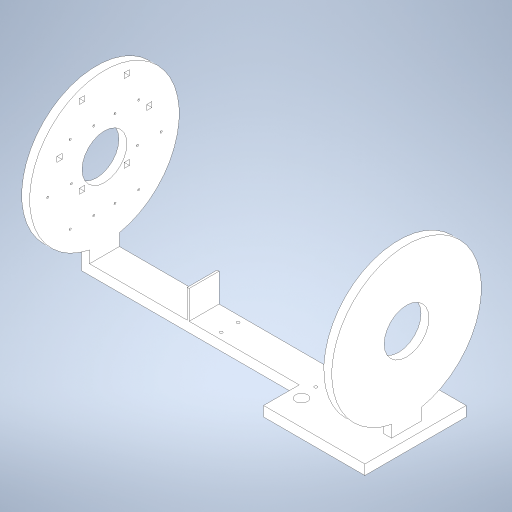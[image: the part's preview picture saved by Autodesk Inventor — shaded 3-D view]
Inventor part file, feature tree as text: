
AUTODESK INVENTOR PART (.ipt)
format: ipt  version: 2023 (Build 270158000, 158)  size: 558,592 bytes
history: native  units: in
note: dims shown in document units (in); Inventor stores cm internally (conversion verified against a paired STEP export)
features: extrude x12, sketch x5, projected_geometry x2, pattern_linear x1
ambient origin geometry x8: Origin, YZ Plane, XZ Plane, XY Plane, X Axis, Y Axis, Z Axis, Center Point
bodies: Solid1 (feature_tree)
feature tree (20):
  extrude  "Extrusion1"  Depth=0.2047in
  extrude  "Extrusion2"  Depth=0.2047in TaperAngle=360.0deg
  extrude  "Extrusion3"  Depth=0.315in
  sketch  "Sketch2"  dims[d31=0.2047in d32=2.3622in d34=360.0deg]
  extrude  "Extrusion4"  Depth=0.2047in
  extrude  "Extrusion5"  Depth=0.315in
  pattern_linear  "Rectangular Pattern1"  Spacing1=0.2047in  [1 undecoded]
  extrude  "Extrusion7"  Depth=0.2047in
  extrude  "Extrusion8"  Depth=0.2717in
  extrude  "Extrusion9"  Depth=0.2717in
  sketch  "Sketch7"  dims[d40=0.315in d41=0.315in d42=0.2047in d43=0.2047in d44=0.8465in d45=4.3307in d46=2.7559in d47=0.5906in d49=0.315in d50=1.122in d51=0.3937in d52=0.315in d53=0.0in d54=0.3937in d55=0.0in d56=12.5984in d57=0.0in d58=4.0in d59=4.0in d60=0.4724in d63=0.2559in d65=3.937in d66=1.0039in d67=0.3346in d68=0.1181in d69=0.7874in d71=3.7402in d72=0.3937in d74=0.3937in d76=0.3937in d77=0.0in d78=0.3937in d79=0.0in d80=1.0in d81=0.5in d82=3.0118in d83=0.3937in d84=0.0in d85=0.7874in d87=11.9291in d88=0.122in d89=0.0in d90=0.122in d91=0.0in d92=0.0787in d93=1.5157in d94=0.0in d95=2.3622in d97=360.0deg d99=120.0deg d102=120.0deg d105=120.0deg d108=1.7717in d109=5.9055in d110=0.315in d111=0.0in d112=1.7717in d113=5.9055in d114=0.3937in d115=0.0in d116=0.2717in d117=0.0in d118=0.9843in d119=0.7283in d120=0.0827in d122=0.5413in d123=2.3622in d125=360.0deg d127=0.0827in d128=0.5413in d129=0.0827in d130=0.5413in]
  extrude  "Extrusion11"  Depth=0.2717in
  extrude  "Extrusion12"  Depth=0.2717in
  extrude  "Extrusion10"  Depth=0.315in
  extrude  "Extrusion6"  Depth=1.122in
  sketch  "Sketch3"  dims[d36=0.315in d37=0.315in]
  projected_geometry  "Projected Loop1"
  sketch  "Sketch4"  dims[d38=0.2047in d39=0.2047in]
  projected_geometry  "Projected Loop2"
  sketch  "Sketch1"  dims[d8=1.378in d9=1.7717in d12=1.1811in d13=0.315in d14=0.315in d22=1.1811in d23=0.315in d24=1.1811in d25=1.378in d26=1.378in d27=0.1575in d30=0.2047in]
note: 1 required parameter value undecoded (feature->parameter linkage not recoverable at this tier; creation-order binding heuristic only, values carry confidence <= 0.55)
